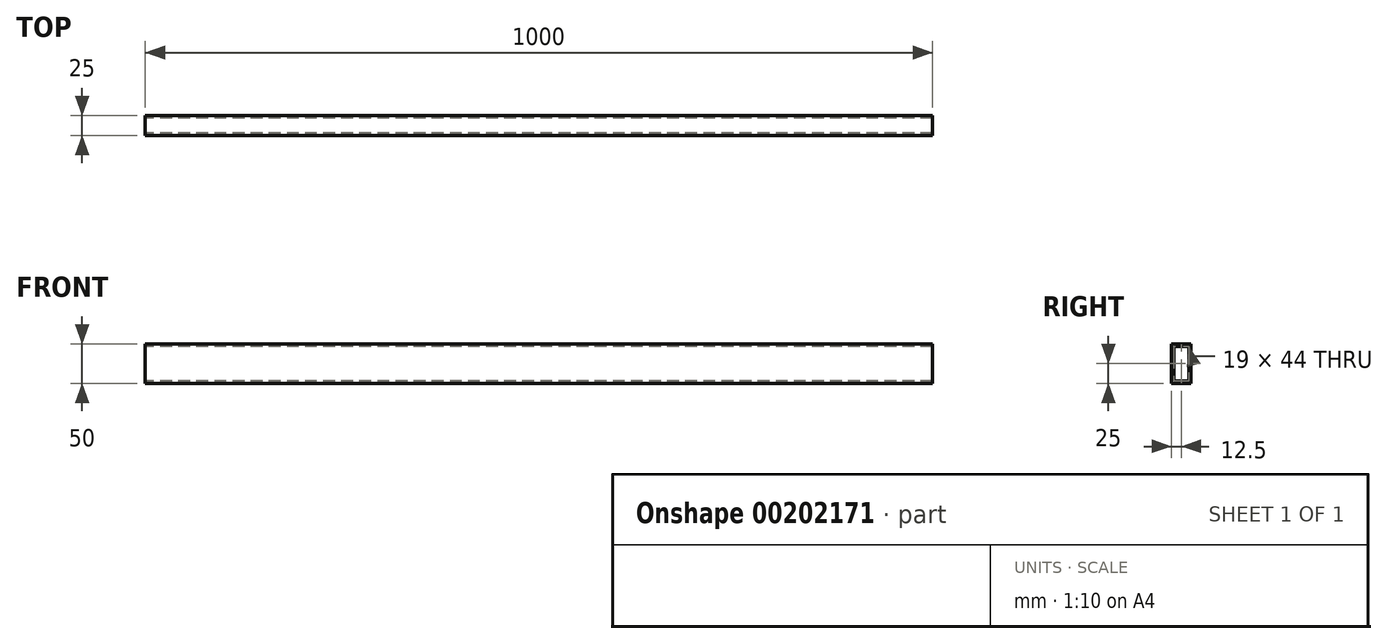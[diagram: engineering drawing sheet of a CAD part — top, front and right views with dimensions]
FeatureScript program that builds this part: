
annotation { "Feature Type Name" : "Feature", "Feature Type Description" : "" }
export const myFeature = defineFeature(function(context is Context, id is Id, definition is map)
    precondition{}
    {
        {
            var Q0;
            Q0=qCreatedBy(makeId("Front.planeOp"),FACE);
            var sketch = newSketch(context, id + "F0", { "sketchPlane" : qUnion([Q0])});
            skLineSegment(sketch, "E0.bottom", {"start": v(500, 25) * mm, "end": v(-500, 25) * mm});
            skLineSegment(sketch, "E0.top", {"start": v(500, -25) * mm, "end": v(-500, -25) * mm});
            skLineSegment(sketch, "E0.left", {"start": v(500, 25) * mm, "end": v(500, -25) * mm});
            skLineSegment(sketch, "E0.right", {"start": v(-500, 25) * mm, "end": v(-500, -25) * mm});
            skPoint(sketch, "E0.middle", {"position": v(0, 0) * mm});
            skSolve(sketch);
        }
        {
            var Q0;
            Q0=qSketchRegion(id+"F0",true);
            extrude(context, id + "F1", {"entities" : qUnion([Q0]), "depth" : 25 * mm});
        }
        {
            var Q0;
            Q0=makeQuery(id+"F1.opExtrude","SWEPT_FACE",FACE,{"disambiguationData":[OSD([sQuery(id+"F0.wireOp",EDGE,"E0.right")])]});
            var sketch = newSketch(context, id + "F2", { "sketchPlane" : qUnion([Q0])});
            skLineSegment(sketch, "E1.0", {"start": v(22, 22) * mm, "end": v(3, 22) * mm});
            skLineSegment(sketch, "E1.1", {"start": v(22, 22) * mm, "end": v(22, -22) * mm});
            skLineSegment(sketch, "E1.2", {"start": v(22, -22) * mm, "end": v(3, -22) * mm});
            skLineSegment(sketch, "E2.0", {"start": v(3, 22) * mm, "end": v(3, -22) * mm});
            skSolve(sketch);
        }
        {
            var Q0;
            Q0=qSketchRegion(id+"F2",true);
            extrude(context, id + "F3", {"entities" : qUnion([Q0]), "operationType" : NewBodyOperationType.REMOVE, "oppositeDirection" : true, "depth" : 1130 * mm});
        }
    });
